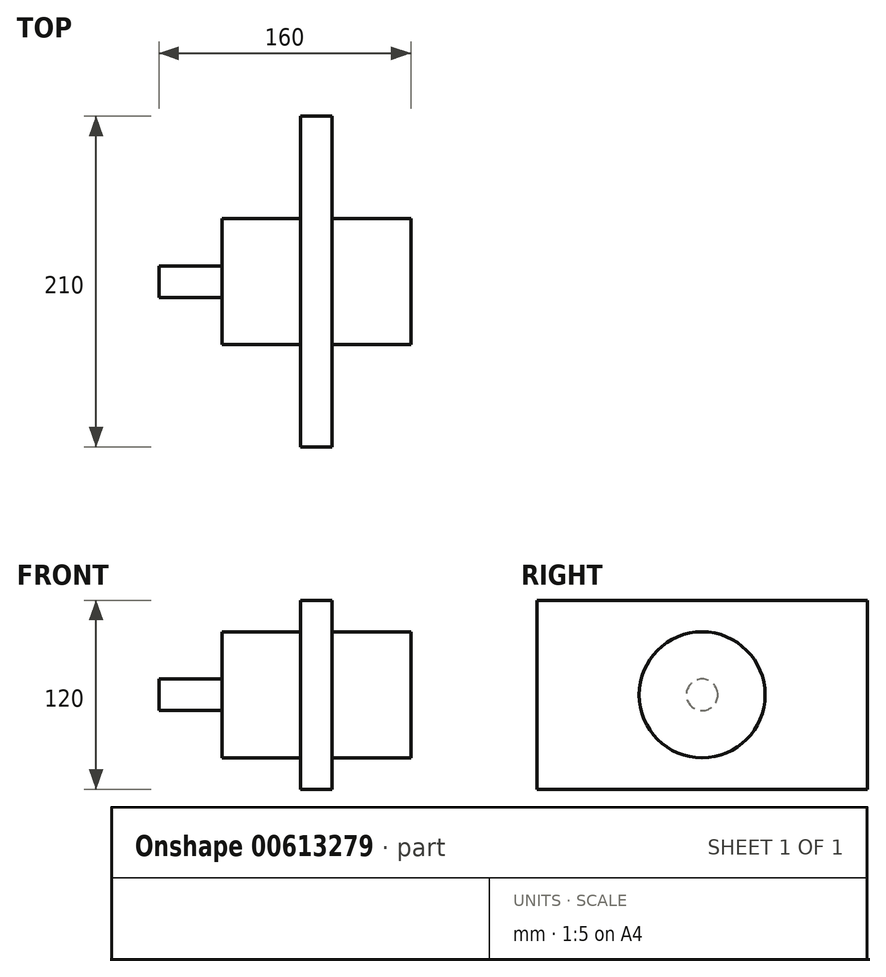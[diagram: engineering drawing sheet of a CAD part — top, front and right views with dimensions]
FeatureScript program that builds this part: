
annotation { "Feature Type Name" : "Feature", "Feature Type Description" : "" }
export const myFeature = defineFeature(function(context is Context, id is Id, definition is map)
    precondition{}
    {
        {
            var Q0;
            Q0=qCreatedBy(makeId("Right.planeOp"),FACE);
            var sketch = newSketch(context, id + "F0", { "sketchPlane" : qUnion([Q0])});
            skLineSegment(sketch, "E0.bottom", {"start": v(105, -60) * mm, "end": v(-105, -60) * mm});
            skLineSegment(sketch, "E0.top", {"start": v(105, 60) * mm, "end": v(-105, 60) * mm});
            skLineSegment(sketch, "E0.left", {"start": v(105, -60) * mm, "end": v(105, 60) * mm});
            skLineSegment(sketch, "E0.right", {"start": v(-105, -60) * mm, "end": v(-105, 60) * mm});
            skPoint(sketch, "E0.middle", {"position": v(0, 0) * mm});
            skSolve(sketch);
        }
        {
            var Q0;
            Q0 = qSketchRegion(id + "F0", true);
            extrude(context, id + "F1", {"entities" : qUnion([Q0]), "depth" : 20 * mm, "offsetDistance" : 25 * mm});
        }
        {
            var Q0;
            Q0=makeQuery(id+"F1.opExtrude","CAP_FACE",FACE,{"disambiguationData":[OSD([sQuery(id+"F0.wireOp",EDGE,"E0.bottom"),sQuery(id+"F0.wireOp",EDGE,"E0.top"),sQuery(id+"F0.wireOp",EDGE,"E0.left"),sQuery(id+"F0.wireOp",EDGE,"E0.right")])],"isStart":false});
            var sketch = newSketch(context, id + "F2", { "sketchPlane" : qUnion([Q0])});
            skCircle(sketch, "E1", {"center": v(0, 0) * mm, "radius": 40 * mm});
            skSolve(sketch);
        }
        {
            var Q0;
            Q0=makeQuery(id+"F2.imprint","IMPRINT",FACE,{"disambiguationData":[TD([[makeQuery(id+"F2.imprint","IMPRINT",EDGE,{"derivedFrom":sQuery(id+"F2.wireOp",EDGE,"E1")}),1.0]])]});
            extrude(context, id + "F3", {"entities" : qUnion([Q0]), "operationType" : NewBodyOperationType.ADD, "depth" : 50 * mm, "offsetDistance" : 25 * mm});
        }
        {
            var Q0;
            Q0=makeQuery(id+"F1.opExtrude","CAP_FACE",FACE,{"disambiguationData":[OSD([sQuery(id+"F0.wireOp",EDGE,"E0.bottom"),sQuery(id+"F0.wireOp",EDGE,"E0.top"),sQuery(id+"F0.wireOp",EDGE,"E0.left"),sQuery(id+"F0.wireOp",EDGE,"E0.right")])],"isStart":true});
            var sketch = newSketch(context, id + "F4", { "sketchPlane" : qUnion([Q0])});
            skCircle(sketch, "E2", {"center": v(0, 0) * mm, "radius": 40 * mm});
            skSolve(sketch);
        }
        {
            var Q0;
            Q0=makeQuery(id+"F4.imprint","IMPRINT",FACE,{"disambiguationData":[TD([[makeQuery(id+"F4.imprint","IMPRINT",EDGE,{"derivedFrom":sQuery(id+"F4.wireOp",EDGE,"E2")}),1.0]])]});
            extrude(context, id + "F5", {"entities" : qUnion([Q0]), "operationType" : NewBodyOperationType.ADD, "depth" : 50 * mm, "offsetDistance" : 25 * mm});
        }
        {
            var Q0;
            Q0=makeQuery(id+"F5.opExtrude","CAP_FACE",FACE,{"disambiguationData":[OSD([sQuery(id+"F4.wireOp",EDGE,"E2")])],"isStart":false});
            var sketch = newSketch(context, id + "F6", { "sketchPlane" : qUnion([Q0])});
            skCircle(sketch, "E3", {"center": v(0, 0) * mm, "radius": 10 * mm});
            skSolve(sketch);
        }
        {
            var Q0;
            Q0 = qSketchRegion(id + "F6", true);
            extrude(context, id + "F7", {"entities" : qUnion([Q0]), "operationType" : NewBodyOperationType.ADD, "depth" : 40 * mm, "offsetDistance" : 25 * mm});
        }
    });
